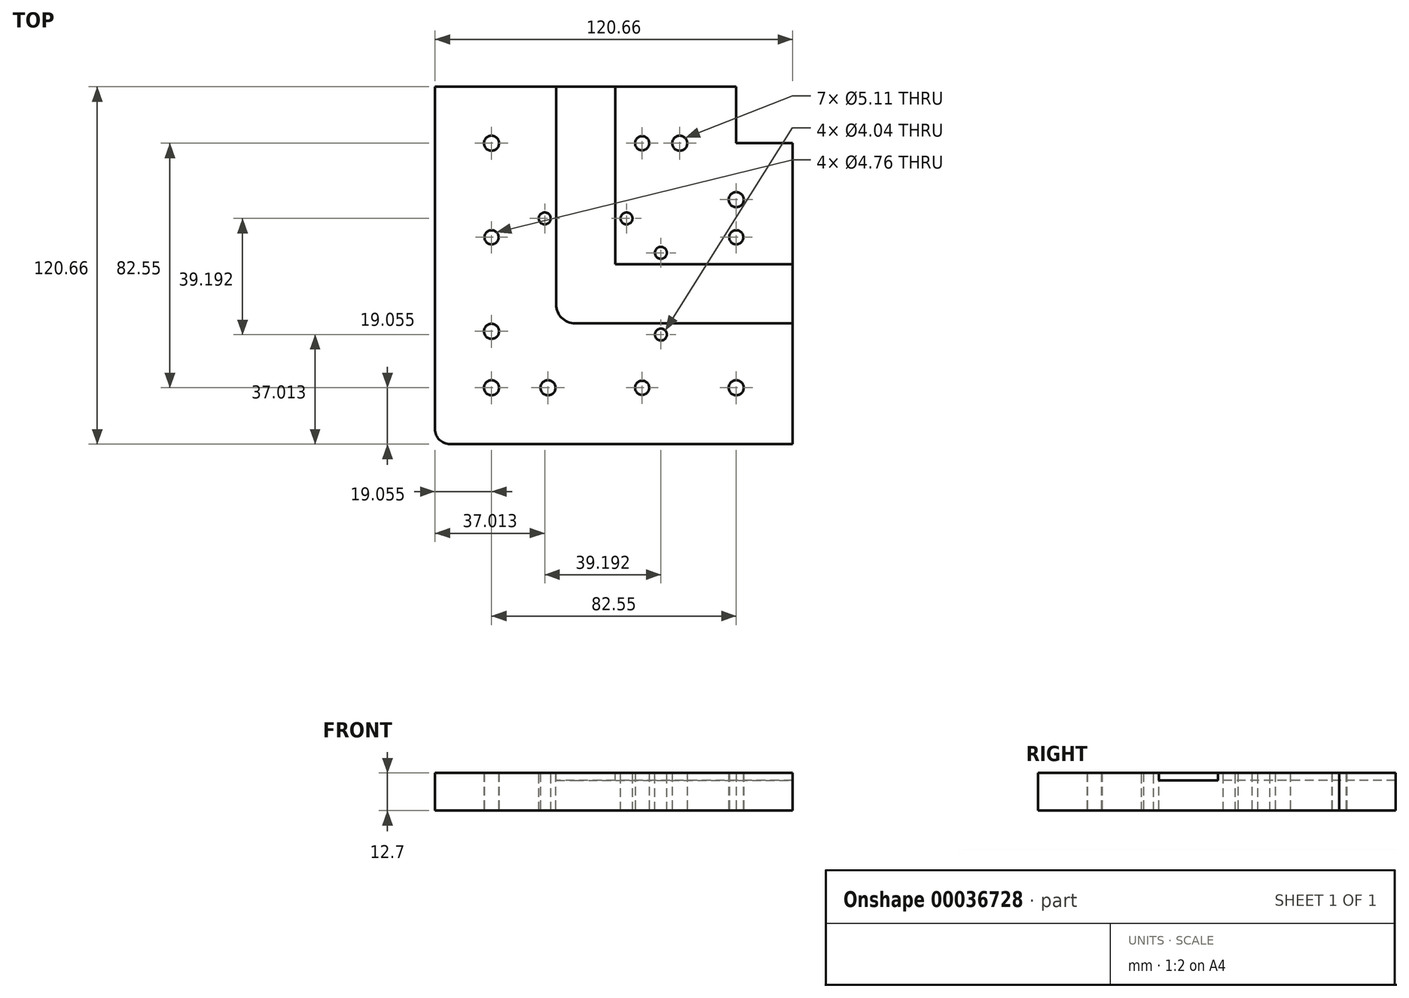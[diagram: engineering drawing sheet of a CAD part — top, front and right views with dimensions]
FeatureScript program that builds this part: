
annotation { "Feature Type Name" : "Feature", "Feature Type Description" : "" }
export const myFeature = defineFeature(function(context is Context, id is Id, definition is map)
    precondition{}
    {
        {
            var Q0;
            Q0=qCreatedBy(makeId("Top.planeOp"),FACE);
            var sketch = newSketch(context, id + "F0", { "sketchPlane" : qUnion([Q0])});
            skLineSegment(sketch, "E0.bottom", {"start": v(41.28, 60.33) * mm, "end": v(-60.33, 60.33) * mm});
            skLineSegment(sketch, "E0.top", {"start": v(60.32, -60.33) * mm, "end": v(-60.32, -60.33) * mm});
            skLineSegment(sketch, "E0.left", {"start": v(60.33, 41.28) * mm, "end": v(60.33, -60.32) * mm});
            skLineSegment(sketch, "E0.right", {"start": v(-60.33, 60.33) * mm, "end": v(-60.32, -60.32) * mm});
            skPoint(sketch, "E0.middle", {"position": v(0, 0) * mm});
            skLineSegment(sketch, "E1.top", {"start": v(60.33, 41.28) * mm, "end": v(41.28, 41.28) * mm});
            skLineSegment(sketch, "E1.right", {"start": v(41.28, 60.33) * mm, "end": v(41.28, 41.28) * mm});
            skPoint(sketch, "E2.orphan", {"position": v(60.32, 60.33) * mm});
            skSolve(sketch);
        }
        {
            var Q0;
            Q0 = qSketchRegion(id + "F0", true);
            extrude(context, id + "F1", {"entities" : qUnion([Q0]), "depth" : 12.7 * mm});
        }
        {
            var Q0;
            Q0=makeQuery(id+"F1.opExtrude","CAP_FACE",FACE,{"disambiguationData":[OSD([sQuery(id+"F0.wireOp",EDGE,"E0.bottom"),sQuery(id+"F0.wireOp",EDGE,"E0.top"),sQuery(id+"F0.wireOp",EDGE,"E0.left"),sQuery(id+"F0.wireOp",EDGE,"E0.right"),sQuery(id+"F0.wireOp",EDGE,"E1.top"),sQuery(id+"F0.wireOp",EDGE,"E1.right")])],"isStart":false});
            var sketch = newSketch(context, id + "F2", { "sketchPlane" : qUnion([Q0])});
            skLineSegment(sketch, "E3", {"start": v(-19.5, 60.33) * mm, "end": v(-19.5, -19.5) * mm});
            skLineSegment(sketch, "E4", {"start": v(-19.5, -19.5) * mm, "end": v(60.33, -19.5) * mm});
            skLineSegment(sketch, "E5", {"start": v(60.33, -19.5) * mm, "end": v(60.33, 0.46) * mm});
            skLineSegment(sketch, "E6", {"start": v(60.33, 0.46) * mm, "end": v(0.46, 0.46) * mm});
            skLineSegment(sketch, "E7", {"start": v(0.46, 0.46) * mm, "end": v(0.46, 60.33) * mm});
            skLineSegment(sketch, "E8", {"start": v(0.46, 60.33) * mm, "end": v(-19.5, 60.33) * mm});
            skLineSegment(sketch, "E9", {"start": v(-9.52, 60.33) * mm, "end": v(-9.52, -9.52) * mm, "construction": true});
            skLineSegment(sketch, "E10", {"start": v(60.33, -9.52) * mm, "end": v(-9.52, -9.52) * mm, "construction": true});
            skSolve(sketch);
        }
        {
            var Q0;
            Q0 = qSketchRegion(id + "F2", true);
            extrude(context, id + "F3", {"entities" : qUnion([Q0]), "operationType" : NewBodyOperationType.REMOVE, "oppositeDirection" : true, "depth" : 2.54 * mm});
        }
        {
            var Q0;
            Q0=makeQuery(id+"F1.opExtrude","CAP_FACE",FACE,{"disambiguationData":[OSD([sQuery(id+"F0.wireOp",EDGE,"E0.bottom"),sQuery(id+"F0.wireOp",EDGE,"E0.top"),sQuery(id+"F0.wireOp",EDGE,"E0.left"),sQuery(id+"F0.wireOp",EDGE,"E0.right"),sQuery(id+"F0.wireOp",EDGE,"E1.top"),sQuery(id+"F0.wireOp",EDGE,"E1.right")])],"isStart":true});
            var sketch = newSketch(context, id + "F4", { "sketchPlane" : qUnion([Q0])});
            skPoint(sketch, "E11", {"position": v(-22.22, 41.28) * mm});
            skPoint(sketch, "E12", {"position": v(41.27, -22.23) * mm});
            skPoint(sketch, "E13", {"position": v(41.28, 41.28) * mm});
            skPoint(sketch, "E14", {"position": v(-41.27, 22.23) * mm});
            skPoint(sketch, "E15", {"position": v(22.23, -41.28) * mm});
            skPoint(sketch, "E16", {"position": v(-41.27, -41.28) * mm});
            skSolve(sketch);
        }
        {
            var Q0;
            Q0=sQuery(id+"F4.wireOp",VERTEX,"E16");
            var Q1;
            Q1=sQuery(id+"F4.wireOp",VERTEX,"E15");
            var Q2;
            Q2=sQuery(id+"F4.wireOp",VERTEX,"E12");
            var Q3;
            Q3=sQuery(id+"F4.wireOp",VERTEX,"E13");
            var Q4;
            Q4=sQuery(id+"F4.wireOp",VERTEX,"E11");
            var Q5;
            Q5=sQuery(id+"F4.wireOp",VERTEX,"E14");
            var Q6;
            Q6=makeQuery(id+"F1.opExtrude","SWEPT_BODY",BODY,{"disambiguationData":[OSD([sQuery(id+"F0.wireOp",EDGE,"E0.bottom"),sQuery(id+"F0.wireOp",EDGE,"E0.top"),sQuery(id+"F0.wireOp",EDGE,"E0.left"),sQuery(id+"F0.wireOp",EDGE,"E0.right"),sQuery(id+"F0.wireOp",EDGE,"E1.top"),sQuery(id+"F0.wireOp",EDGE,"E1.right")])]});
            hole(context, id + "F5", {"style" : HoleStyle.SIMPLE, "endStyle" : HoleEndStyle.THROUGH, "standardTappedOrClearance" : lookupTablePath({ "standard" : "ANSI", "engagement" : "75%", "pitch" : "20 tpi", "size" : "1/4", "type" : "Tapped" }), "standardBlindInLast" : lookupTablePath({ "standard" : "ANSI", "engagement" : "75%", "pitch" : "20 tpi", "size" : "1/4", "type" : "Tapped" }), "holeDiameter" : 5.1 * mm, "showTappedDepth" : true, "tappedDepth" : 6.35 * mm, "tapClearance" : 3, "locations" : qUnion([Q0, Q1, Q2, Q3, Q4, Q5]), "scope" : qUnion([Q6]), "majorDiameter" : 6.35 * mm});
        }
        {
            var Q0;
            {var subQ0=sQuery(id+"F0.wireOp",EDGE,"E0.left");var subQ1=sQuery(id+"F0.wireOp",EDGE,"E0.top");var subQ2=sQuery(id+"F0.wireOp",EDGE,"E0.right");var subQ3=sQuery(id+"F0.wireOp",EDGE,"E0.bottom");Q0=makeQuery(id+"F3.boolean.opBoolean","SPLIT",FACE,{"disambiguationData":[TD([makeQuery(id+"F1.opExtrude","SWEPT_FACE",FACE,{"disambiguationData":[OSD([subQ1])]})])],"derivedFrom":makeQuery(id+"F1.opExtrude","CAP_FACE",FACE,{"disambiguationData":[OSD([subQ3,subQ1,subQ0,subQ2,sQuery(id+"F0.wireOp",EDGE,"E1.top"),sQuery(id+"F0.wireOp",EDGE,"E1.right")])],"isStart":false})});}
            var sketch = newSketch(context, id + "F6", { "sketchPlane" : qUnion([Q0])});
            skPoint(sketch, "E17", {"position": v(15.88, 4.27) * mm});
            skPoint(sketch, "E18", {"position": v(15.88, -23.32) * mm});
            skPoint(sketch, "E19", {"position": v(4.27, 15.88) * mm});
            skPoint(sketch, "E20", {"position": v(-23.32, 15.88) * mm});
            skSolve(sketch);
        }
        {
            var Q0;
            Q0=sQuery(id+"F6.wireOp",VERTEX,"E19");
            var Q1;
            Q1=sQuery(id+"F6.wireOp",VERTEX,"E20");
            var Q2;
            Q2=sQuery(id+"F6.wireOp",VERTEX,"E17");
            var Q3;
            Q3=sQuery(id+"F6.wireOp",VERTEX,"E18");
            var Q4;
            Q4=makeQuery(id+"F1.opExtrude","SWEPT_BODY",BODY,{"disambiguationData":[OSD([sQuery(id+"F0.wireOp",EDGE,"E0.bottom"),sQuery(id+"F0.wireOp",EDGE,"E0.top"),sQuery(id+"F0.wireOp",EDGE,"E0.left"),sQuery(id+"F0.wireOp",EDGE,"E0.right"),sQuery(id+"F0.wireOp",EDGE,"E1.top"),sQuery(id+"F0.wireOp",EDGE,"E1.right")])]});
            hole(context, id + "F7", {"style" : HoleStyle.SIMPLE, "endStyle" : HoleEndStyle.THROUGH, "standardTappedOrClearance" : lookupTablePath({ "standard" : "ANSI", "engagement" : "75%", "pitch" : "32 tpi", "size" : "#10", "type" : "Tapped" }), "standardBlindInLast" : lookupTablePath({ "standard" : "ANSI", "engagement" : "75%", "pitch" : "32 tpi", "size" : "#10", "type" : "Tapped" }), "holeDiameter" : 4.04 * mm, "showTappedDepth" : true, "tappedDepth" : 6.35 * mm, "tapClearance" : 3, "locations" : qUnion([Q0, Q1, Q2, Q3]), "scope" : qUnion([Q4]), "majorDiameter" : 4.83 * mm});
        }
        {
            var Q0;
            Q0=makeQuery(id+"F1.opExtrude","CAP_FACE",FACE,{"disambiguationData":[OSD([sQuery(id+"F0.wireOp",EDGE,"E0.bottom"),sQuery(id+"F0.wireOp",EDGE,"E0.top"),sQuery(id+"F0.wireOp",EDGE,"E0.left"),sQuery(id+"F0.wireOp",EDGE,"E0.right"),sQuery(id+"F0.wireOp",EDGE,"E1.top"),sQuery(id+"F0.wireOp",EDGE,"E1.right")])],"isStart":true});
            var sketch = newSketch(context, id + "F8", { "sketchPlane" : qUnion([Q0])});
            skPoint(sketch, "E21", {"position": v(-41.27, 41.28) * mm});
            skSolve(sketch);
        }
        {
            var Q0;
            Q0=sQuery(id+"F8.wireOp",VERTEX,"E21");
            var Q1;
            Q1=makeQuery(id+"F1.opExtrude","SWEPT_BODY",BODY,{"disambiguationData":[OSD([sQuery(id+"F0.wireOp",EDGE,"E0.bottom"),sQuery(id+"F0.wireOp",EDGE,"E0.top"),sQuery(id+"F0.wireOp",EDGE,"E0.left"),sQuery(id+"F0.wireOp",EDGE,"E0.right"),sQuery(id+"F0.wireOp",EDGE,"E1.top"),sQuery(id+"F0.wireOp",EDGE,"E1.right")])]});
            hole(context, id + "F9", {"style" : HoleStyle.SIMPLE, "endStyle" : HoleEndStyle.THROUGH, "standardTappedOrClearance" : lookupTablePath({ "standard" : "ANSI", "engagement" : "75%", "pitch" : "20 tpi", "size" : "1/4", "type" : "Tapped" }), "standardBlindInLast" : lookupTablePath({ "standard" : "ANSI", "engagement" : "75%", "pitch" : "20 tpi", "size" : "1/4", "type" : "Tapped" }), "holeDiameter" : 5.1 * mm, "showTappedDepth" : true, "isTappedThrough" : true, "tappedDepth" : 6.35 * mm, "tapClearance" : 3, "locations" : qUnion([Q0]), "scope" : qUnion([Q1]), "majorDiameter" : 6.35 * mm});
        }
        {
            var Q0;
            Q0=makeQuery(id+"F1.opExtrude","CAP_FACE",FACE,{"disambiguationData":[OSD([sQuery(id+"F0.wireOp",EDGE,"E0.bottom"),sQuery(id+"F0.wireOp",EDGE,"E0.top"),sQuery(id+"F0.wireOp",EDGE,"E0.left"),sQuery(id+"F0.wireOp",EDGE,"E0.right"),sQuery(id+"F0.wireOp",EDGE,"E1.top"),sQuery(id+"F0.wireOp",EDGE,"E1.right")])],"isStart":true});
            var sketch = newSketch(context, id + "F10", { "sketchPlane" : qUnion([Q0])});
            skCircle(sketch, "E22", {"center": v(9.53, 41.28) * mm, "radius": 2.38 * mm});
            skCircle(sketch, "E23", {"center": v(41.28, -9.53) * mm, "radius": 2.38 * mm});
            skCircle(sketch, "E24", {"center": v(9.53, -41.28) * mm, "radius": 2.38 * mm});
            skCircle(sketch, "E25", {"center": v(-41.27, -9.53) * mm, "radius": 2.38 * mm});
            skLineSegment(sketch, "E26", {"start": v(-22.22, 41.28) * mm, "end": v(41.28, 41.28) * mm, "construction": true});
            skLineSegment(sketch, "E27", {"start": v(41.28, 41.28) * mm, "end": v(41.27, -22.23) * mm, "construction": true});
            skLineSegment(sketch, "E28", {"start": v(22.23, -41.28) * mm, "end": v(-41.27, -41.28) * mm, "construction": true});
            skLineSegment(sketch, "E29", {"start": v(-41.27, -41.28) * mm, "end": v(-41.27, 22.22) * mm, "construction": true});
            skSolve(sketch);
        }
        {
            var Q0;
            Q0 = qSketchRegion(id + "F10", true);
            extrude(context, id + "F11", {"entities" : qUnion([Q0]), "operationType" : NewBodyOperationType.REMOVE, "endBound" : BoundingType.THROUGH_ALL, "oppositeDirection" : true, "depth" : 25.4 * mm});
        }
        {
            var Q0;
            Q0=makeQuery(id+"F3.boolean.opBoolean","COPY",EDGE,{"derivedFrom":makeQuery(id+"F3.opExtrude","SWEPT_EDGE",EDGE,{"disambiguationData":[OSD([sQuery(id+"F2.wireOp",EDGE,"E3"),sQuery(id+"F2.wireOp",EDGE,"E4")])]})});
            fillet(context, id + "F12", {"entities" : qUnion([Q0]), "radius" : 6.35 * mm, "tangentPropagation" : true, "allowEdgeOverflow" : false});
        }
        {
            var Q0;
            Q0=makeQuery(id+"F1.opExtrude","SWEPT_EDGE",EDGE,{"disambiguationData":[OSD([sQuery(id+"F0.wireOp",EDGE,"E0.top"),sQuery(id+"F0.wireOp",EDGE,"E0.right")])]});
            fillet(context, id + "F13", {"entities" : qUnion([Q0]), "radius" : 5.08 * mm, "tangentPropagation" : true, "allowEdgeOverflow" : false});
        }
    });
